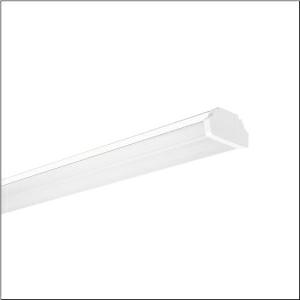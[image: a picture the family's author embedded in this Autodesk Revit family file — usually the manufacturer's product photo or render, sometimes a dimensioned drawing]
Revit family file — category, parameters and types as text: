
# Revit family: dus_r__31_mo_53bd812c1v4075_b8a3
name_source: partatom
category: Lighting Fixtures
units: mm (PartAtom-declared; Revit-internal decimal feet)

## family parameters
Cut with Voids When Loaded = No
Host = Face
Light Source = No
Part Type = Normal
Room Calculation Point = No
Round Connector Dimension = Use Diameter
Shared = No

## types (1)
- --- (1 x LED, 7620 lm, 48.9 W, 4000K)
    Apparent Load = 49 VA
    CIE Flux Codes = 47 80 95 92 100
    Color Rendering = 80
    Color Temperature = 4000K
    Default Elevation = 1800 mm
    Description = DUS® 31 MO, luminaire insert, of sheet steel, coil coated, white, length: 1.535mm, width: 81mm, height: 90mm, 5x system unit, system units: 307mm, LED rated luminous flux: 7.620lm, light colour: 840, control gear: ON/OFF Multilumen, CLOi, control gear: ECG Multilumen, with plug, 3-pole, with phase selection, mains connection: 220..240V, AC, 50/60Hz, start of lifetime: 49W, end of service life: 56W, through-wiring accessed according to module size, primary optical cover: cover, of PMMA, light emission: direct distribution, primary light characteristic: symmetric, protection rating (complete): IP20, protection rating (LED compartment): IP50, insulation class (complete): insulation class I (protective earthing), certification: CE, ENEC, VDE, UKCA, impact resistance: IK03, permissible ambient temperature for indoor applications: -35..+30°C, corresponds to IFS (International Featured Standards) requirements for safety and quality in the food industry, reducing of maximum allowable ambient temperature of 5°C with ceiling mounting, packaging unit: 1 piece
    Height = 95 mm
    Lamp = 1 x LED
    Lamp Light Flux = 7620 lm
    Lamp Power = 48.9 W
    Lamp count = 1
    Length = 1535 mm
    Luminous efficacy = 156 lm/W
    Manufacturer = Siteco
    ModVariant = No
    Model = 53BD812C1V4075
    Mounting Place = Ceiling
    Mounting Type = Pendant
    Number of Poles = 1
    OnlyDefault = Yes
    Power Factor = 1
    Product Name = DUS® 31 MO
    Product group = luminaire insert
    ProductGroupID = 901
    Protection Class = Protection class I
    Protection Degree = IP 20
    RLX_Detail_Level = 1
    RLX_Emergency_Light_Flux = 0 lm
    RLX_Emergency_Type = 0
    RLX_Emergency_Type_DB = No
    RlxData = <blob elided: 39785 chars, md5=4930d55c>
    Socket = socket
    Standby Power = 0 W
    System Light Flux = 7620 lm
    System Power = 49 W
    Type Comments = factory setting: luminous flux: 100 % | (A | C | E) | 107 mA
    Type Image = l_1313537.jpg
    URL = http://relux.com
    VarID = @adj_154987
    Voltage = 0 V
    Weight = 0.00 kg
    Width = 81 mm

## geometry (parser evidence)
native form markers: Blend x4, Sweep x13
no freeform markers — native parametric forms only
